# Revit family: MBS_bookcase
name_source: partatom
category: Generic Models
revit_build: Autodesk Revit 2014 (Build: 20130308_1515(x64)
units: mm (PartAtom-declared; Revit-internal decimal feet)

## types (2) — shared parameters
bookcase material = Oak, White BOOKCASE MBS
c_shelf2 widht = 1500 mm  [stored 4.92126 ft]
c_side5 height = 250 mm  [stored 0.82021 ft]
shelves thickness = 50 mm  [stored 0.164042 ft]
support material = Glass, Clear Glazing SUPPORT MBS

## per-type parameters (varying)
| type | c_shelf1 widht | c_shelf3 widht | c_shelf4 widht | c_shelf5 widht | c_shelf6 widht | c_side1 height | c_side2 height | c_side3 height | c_side4 height | shelves depht |
| bookcase1 | 1500 mm  [stored 4.92126 ft] | 900 mm  [stored 2.95276 ft] | 900 mm  [stored 2.95276 ft] | 1200 mm | 900 mm  [stored 2.95276 ft] | 250 mm  [stored 0.82021 ft] | 500 mm  [stored 1.64042 ft] | 300 mm | 200 mm  [stored 0.656168 ft] | 300 mm |
| bookcase2 | 1800 mm  [stored 5.90551 ft] | 1100 mm | 1100 mm | 900 mm  [stored 2.95276 ft] | 600 mm | 150 mm | 600 mm | 150 mm | 350 mm  [stored 1.14829 ft] | 400 mm  [stored 1.31234 ft] |

note: [stored X ft] marks values corroborated as IEEE doubles in the binary element streams (Revit-internal decimal feet)

## geometry (parser evidence)
native form markers: Sweep x1
no freeform markers — native parametric forms only
